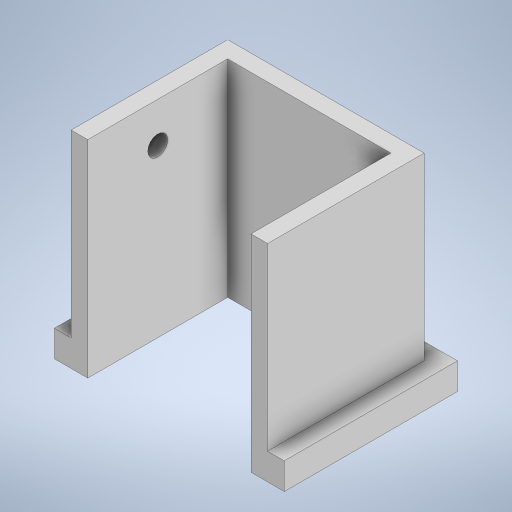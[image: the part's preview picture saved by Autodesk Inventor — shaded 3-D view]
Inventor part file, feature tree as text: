
AUTODESK INVENTOR PART (.ipt)
format: ipt  version: 2023 (Build 270158000, 158)  size: 262,144 bytes
history: native  units: in
note: dims shown in document units (in); Inventor stores cm internally (conversion verified against a paired STEP export)
features: sketch x5, extrude x4
ambient origin geometry x8: Origin, YZ Plane, XZ Plane, XY Plane, X Axis, Y Axis, Z Axis, Center Point
bodies: Solid1 (feature_tree)
feature tree (9):
  extrude  "Extrusion1"  Depth=0.1969in
  extrude  "Extrusion7"  Depth=1.6535in
  extrude  "Extrusion8"  Depth=1.6535in
  sketch  "Sketch9"  dims[d6=2.4409in d7=0.0in d34=0.1969in]
  extrude  "Extrusion9"  Depth=0.1969in
  sketch  "Sketch1"  dims[d0=2.3228in d1=0.1969in]
  sketch  "Sketch7"  dims[d2=0.1969in d3=1.6535in]
  sketch  "Sketch8"  dims[d4=0.1969in d5=1.6535in]
  sketch  "Sketch10"  dims[d35=2.0472in d36=0.1969in d37=2.0472in d38=0.315in d39=0.0in d40=0.3937in d41=0.1969in d42=0.3937in d43=0.1969in d44=1.3583in d47=0.1969in d48=0.1969in d49=0.1969in d50=0.0in d51=0.8268in d52=1.9685in d53=0.2362in d54=0.1969in d55=0.0in d56=0.5118in d57=0.5118in d11=0.0197in d12=0.0344in d13=0.0197in d14=0.0344in]
